# Revit family: KL-4336P70
name_source: partatom
category: Lighting Fixtures
revit_build: Autodesk Revit 2014 (Build: 20130308_1515(x64)
units: mm (PartAtom-declared; Revit-internal decimal feet)

## types (1)
- KL_4300
    Apparent Load = 0 VA
    Assembly Code = D5020200
    Color Filter = 16777215
    Description = The 4300 Sign/Wall Lighter LED utilizes Kim's high performance PicoPrism optics to produce clean, smooth, illumination for sign lighting or wall wash applications. Its compact size makes it easy to conceal behind plants and shrubbery, while offering the latest in LED technology and energy efficiency.
    Diameter = 5 "
    Dimming Lamp Color Temperature Shift = <None>
    Finish = Powder Coat-Kim-Black
    Glass = Glass-KIM-Temper Molded
    Height = 24 "
    Lamp = LED
    Load Classification = Lighting
    Manufacturer = Kim Lighting
    MasterFormat Title = Landscape Lighting, Site Lighting, Walkway Lighting
    Model = Sign/Wall Lighter
    Number of Poles = 1
    Photometric Notes = More IES files download on Photometric Web Link
    Photometric Web File = 4336p70-24l4k.ies
    Photometric Web Link = https://www.hubbell.com
    Power Factor = 1
    Product Documentation Link = https://hubbellcdn.com
    Product Page URL = https://www.hubbell.com
    Radius = 2.5 "
    Series = Sign/Wall Lighter
    Tilt Angle = 90.00°
    Type Comments = Flood Light
    URL = https://www.hubbell.com
    Voltage = 120 V
    W1 = 9.25 "
    W2 = 18.5 "
    Wattage Comments = default
    Width = 37 "

## geometry (parser evidence)
native form markers: Sweep x2
no freeform markers — native parametric forms only
